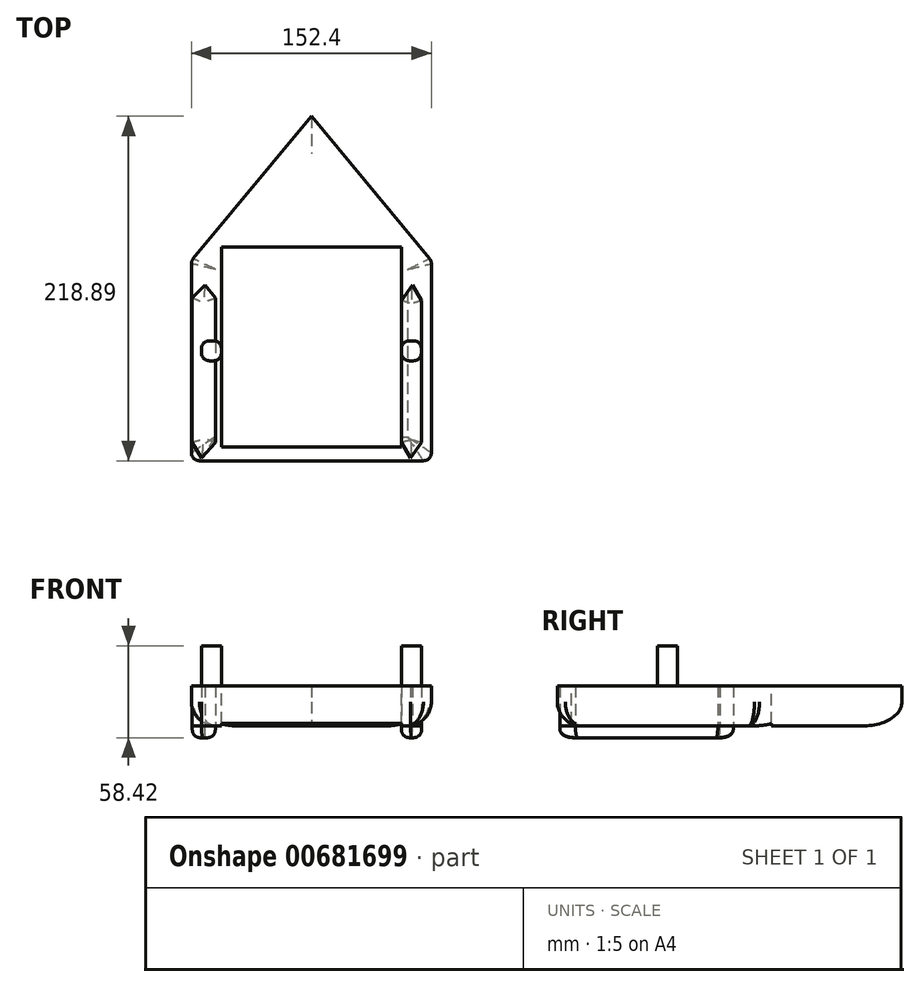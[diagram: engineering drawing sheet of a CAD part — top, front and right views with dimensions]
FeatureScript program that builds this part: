
annotation { "Feature Type Name" : "Feature", "Feature Type Description" : "" }
export const myFeature = defineFeature(function(context is Context, id is Id, definition is map)
    precondition{}
    {
        {
            var Q0;
            Q0=qCreatedBy(makeId("Top.planeOp"),FACE);
            var sketch = newSketch(context, id + "F0", { "sketchPlane" : qUnion([Q0])});
            skLineSegment(sketch, "E0.bottom", {"start": v(-152.4, 91.7) * mm, "end": v(0, 91.7) * mm});
            skLineSegment(sketch, "E0.top", {"start": v(-152.4, -35.3) * mm, "end": v(0, -35.3) * mm});
            skLineSegment(sketch, "E0.left", {"start": v(-152.4, 91.7) * mm, "end": v(-152.4, -35.3) * mm});
            skLineSegment(sketch, "E0.right", {"start": v(0, 91.7) * mm, "end": v(0, -35.3) * mm});
            skLineSegment(sketch, "E1", {"start": v(-76.2, 183.59) * mm, "end": v(-152.4, 91.7) * mm});
            skPoint(sketch, "E1.startSnap0", {"position": v(-76.2, 91.7) * mm});
            skLineSegment(sketch, "E2", {"start": v(-76.2, 183.59) * mm, "end": v(0, 91.7) * mm});
            skSolve(sketch);
        }
        {
            var Q0;
            Q0 = qSketchRegion(id + "F0", true);
            extrude(context, id + "F1", {"entities" : qUnion([Q0]), "depth" : 25.4 * mm, "offsetDistance" : 25.4 * mm});
        }
        {
            var Q0;
            Q0=makeQuery(id+"F1.opExtrude","SWEPT_EDGE",EDGE,{"disambiguationData":[OSD([sQuery(id+"F0.wireOp",EDGE,"E0.bottom"),sQuery(id+"F0.wireOp",EDGE,"E0.right")])]});
            var Q1;
            Q1=makeQuery(id+"F1.opExtrude","SWEPT_EDGE",EDGE,{"disambiguationData":[OSD([sQuery(id+"F0.wireOp",EDGE,"E0.bottom"),sQuery(id+"F0.wireOp",EDGE,"E0.left")])]});
            fillet(context, id + "F2", {"entities" : qUnion([Q0, Q1]), "radius" : 5.08 * mm, "tangentPropagation" : true, "allowEdgeOverflow" : false});
        }
        {
            var Q0;
            Q0=makeQuery(id+"F1.opExtrude","SWEPT_EDGE",EDGE,{"disambiguationData":[OSD([sQuery(id+"F0.wireOp",EDGE,"E0.top"),sQuery(id+"F0.wireOp",EDGE,"E0.right")])]});
            var Q1;
            Q1=makeQuery(id+"F1.opExtrude","SWEPT_EDGE",EDGE,{"disambiguationData":[OSD([sQuery(id+"F0.wireOp",EDGE,"E0.top"),sQuery(id+"F0.wireOp",EDGE,"E0.left")])]});
            fillet(context, id + "F3", {"entities" : qUnion([Q0, Q1]), "radius" : 5.08 * mm, "tangentPropagation" : true, "allowEdgeOverflow" : false});
        }
        {
            var Q0;
            Q0=makeQuery(id+"F1.opExtrude","CAP_EDGE",EDGE,{"disambiguationData":[OSD([sQuery(id+"F0.wireOp",EDGE,"E2")])],"isStart":true});
            fillet(context, id + "F4", {"entities" : qUnion([Q0]), "radius" : 15.24 * mm, "tangentPropagation" : true, "allowEdgeOverflow" : false});
        }
        {
            var Q0;
            Q0=makeQuery(id+"F1.opExtrude","CAP_FACE",FACE,{"disambiguationData":[OSD([sQuery(id+"F0.wireOp",EDGE,"E0.top"),sQuery(id+"F0.wireOp",EDGE,"E0.left"),sQuery(id+"F0.wireOp",EDGE,"E0.right"),sQuery(id+"F0.wireOp",EDGE,"E1"),sQuery(id+"F0.wireOp",EDGE,"E2")])],"isStart":false});
            var sketch = newSketch(context, id + "F5", { "sketchPlane" : qUnion([Q0])});
            skLineSegment(sketch, "E3.bottom", {"start": v(-133.35, 100.59) * mm, "end": v(-19.05, 100.59) * mm});
            skLineSegment(sketch, "E3.top", {"start": v(-133.35, -26.41) * mm, "end": v(-19.05, -26.41) * mm});
            skLineSegment(sketch, "E3.left", {"start": v(-133.35, 100.59) * mm, "end": v(-133.35, -26.41) * mm});
            skLineSegment(sketch, "E3.right", {"start": v(-19.05, 100.59) * mm, "end": v(-19.05, -26.41) * mm});
            skLineSegment(sketch, "E4", {"start": v(-76.2, 100.59) * mm, "end": v(-76.2, -26.41) * mm, "construction": true});
            skSolve(sketch);
        }
        {
            var Q0;
            Q0 = qSketchRegion(id + "F5", true);
            extrude(context, id + "F6", {"entities" : qUnion([Q0]), "operationType" : NewBodyOperationType.REMOVE, "oppositeDirection" : true, "depth" : 55.63 * mm, "offsetDistance" : 25.4 * mm});
        }
        {
            var Q0;
            Q0=makeQuery(id+"F1.opExtrude","CAP_FACE",FACE,{"disambiguationData":[OSD([sQuery(id+"F0.wireOp",EDGE,"E0.top"),sQuery(id+"F0.wireOp",EDGE,"E0.left"),sQuery(id+"F0.wireOp",EDGE,"E0.right"),sQuery(id+"F0.wireOp",EDGE,"E1"),sQuery(id+"F0.wireOp",EDGE,"E2")])],"isStart":false});
            var sketch = newSketch(context, id + "F7", { "sketchPlane" : qUnion([Q0])});
            skLineSegment(sketch, "E5.bottom", {"start": v(-133.35, 40.9) * mm, "end": v(-146.05, 40.9) * mm});
            skLineSegment(sketch, "E5.top", {"start": v(-133.35, 28.2) * mm, "end": v(-146.05, 28.2) * mm});
            skLineSegment(sketch, "E5.left", {"start": v(-133.35, 40.9) * mm, "end": v(-133.35, 28.2) * mm});
            skLineSegment(sketch, "E5.right", {"start": v(-146.05, 40.9) * mm, "end": v(-146.05, 28.2) * mm});
            skLineSegment(sketch, "E6.bottom", {"start": v(-19.05, 40.9) * mm, "end": v(-6.35, 40.9) * mm});
            skLineSegment(sketch, "E6.top", {"start": v(-19.05, 28.2) * mm, "end": v(-6.35, 28.2) * mm});
            skLineSegment(sketch, "E6.left", {"start": v(-19.05, 40.9) * mm, "end": v(-19.05, 28.2) * mm});
            skLineSegment(sketch, "E6.right", {"start": v(-6.35, 40.9) * mm, "end": v(-6.35, 28.2) * mm});
            skSolve(sketch);
        }
        {
            var Q0;
            Q0 = qSketchRegion(id + "F7", true);
            extrude(context, id + "F8", {"entities" : qUnion([Q0]), "operationType" : NewBodyOperationType.ADD, "depth" : 25.4 * mm, "offsetDistance" : 25.4 * mm});
        }
        {
            var Q0;
            Q0=makeQuery(id+"F8.opExtrude","SWEPT_EDGE",EDGE,{"disambiguationData":[OSD([sQuery(id+"F7.wireOp",EDGE,"E5.bottom"),sQuery(id+"F7.wireOp",EDGE,"E5.right")])]});
            var Q1;
            Q1=makeQuery(id+"F8.opExtrude","SWEPT_EDGE",EDGE,{"disambiguationData":[OSD([sQuery(id+"F7.wireOp",EDGE,"E5.top"),sQuery(id+"F7.wireOp",EDGE,"E5.right")])]});
            var Q2;
            Q2=makeQuery(id+"F8.opExtrude","SWEPT_EDGE",EDGE,{"disambiguationData":[OSD([sQuery(id+"F5.wireOp",EDGE,"E3.left"),sQuery(id+"F7.wireOp",EDGE,"E5.top"),sQuery(id+"F7.wireOp",EDGE,"E5.left")])]});
            var Q3;
            Q3=makeQuery(id+"F8.opExtrude","SWEPT_EDGE",EDGE,{"disambiguationData":[OSD([sQuery(id+"F5.wireOp",EDGE,"E3.left"),sQuery(id+"F7.wireOp",EDGE,"E5.bottom"),sQuery(id+"F7.wireOp",EDGE,"E5.left")])]});
            fillet(context, id + "F9", {"entities" : qUnion([Q0, Q1, Q2, Q3]), "radius" : 5.08 * mm, "tangentPropagation" : true, "allowEdgeOverflow" : false});
        }
        {
            var Q0;
            Q0=makeQuery(id+"F8.opExtrude","SWEPT_EDGE",EDGE,{"disambiguationData":[OSD([sQuery(id+"F7.wireOp",EDGE,"E6.top"),sQuery(id+"F7.wireOp",EDGE,"E6.right")])]});
            var Q1;
            Q1=makeQuery(id+"F8.opExtrude","SWEPT_EDGE",EDGE,{"disambiguationData":[OSD([sQuery(id+"F7.wireOp",EDGE,"E6.bottom"),sQuery(id+"F7.wireOp",EDGE,"E6.right")])]});
            var Q2;
            Q2=makeQuery(id+"F8.opExtrude","SWEPT_EDGE",EDGE,{"disambiguationData":[OSD([sQuery(id+"F5.wireOp",EDGE,"E3.right"),sQuery(id+"F7.wireOp",EDGE,"E6.top"),sQuery(id+"F7.wireOp",EDGE,"E6.left")])]});
            var Q3;
            Q3=makeQuery(id+"F8.opExtrude","SWEPT_EDGE",EDGE,{"disambiguationData":[OSD([sQuery(id+"F5.wireOp",EDGE,"E3.right"),sQuery(id+"F7.wireOp",EDGE,"E6.bottom"),sQuery(id+"F7.wireOp",EDGE,"E6.left")])]});
            fillet(context, id + "F10", {"entities" : qUnion([Q0, Q1, Q2, Q3]), "radius" : 5.08 * mm, "tangentPropagation" : true, "allowEdgeOverflow" : false});
        }
        {
            var Q0;
            Q0=qCreatedBy(makeId("Top.planeOp"),FACE);
            var sketch = newSketch(context, id + "F11", { "sketchPlane" : qUnion([Q0])});
            skLineSegment(sketch, "E7", {"start": v(-13.13, -33.57) * mm, "end": v(-19.05, -23.7) * mm});
            skLineSegment(sketch, "E8", {"start": v(-19.05, -23.7) * mm, "end": v(-19.05, 66.55) * mm});
            skLineSegment(sketch, "E9", {"start": v(-19.05, 66.55) * mm, "end": v(-12.15, 76.4) * mm});
            skLineSegment(sketch, "E10", {"start": v(-12.15, 76.4) * mm, "end": v(-6.23, 66.55) * mm});
            skLineSegment(sketch, "E11", {"start": v(-6.23, 66.55) * mm, "end": v(-6.23, -23.7) * mm});
            skLineSegment(sketch, "E12", {"start": v(-6.23, -23.7) * mm, "end": v(-13.13, -33.57) * mm});
            skLineSegment(sketch, "E13", {"start": v(-143.66, 76.4) * mm, "end": v(-137.24, 68.04) * mm});
            skLineSegment(sketch, "E14", {"start": v(-137.24, 68.04) * mm, "end": v(-137.24, -23.7) * mm});
            skLineSegment(sketch, "E15", {"start": v(-137.24, -23.7) * mm, "end": v(-145.92, -33.57) * mm});
            skLineSegment(sketch, "E16", {"start": v(-145.92, -33.57) * mm, "end": v(-151.84, -23.7) * mm});
            skLineSegment(sketch, "E17", {"start": v(-151.84, -23.7) * mm, "end": v(-151.84, 68.04) * mm});
            skLineSegment(sketch, "E18", {"start": v(-151.84, 68.04) * mm, "end": v(-143.66, 76.4) * mm});
            skSolve(sketch);
        }
        {
            var Q0;
            Q0 = qSketchRegion(id + "F11", true);
            extrude(context, id + "F12", {"entities" : qUnion([Q0]), "operationType" : NewBodyOperationType.ADD, "oppositeDirection" : true, "depth" : 7.62 * mm, "offsetDistance" : 25.4 * mm});
        }
        {
            var Q0;
            Q0=makeQuery(id+"F12.opExtrude","CAP_EDGE",EDGE,{"disambiguationData":[OSD([sQuery(id+"F11.wireOp",EDGE,"tmOqJ6vF-TFOI-Q0Wm-q9Of-ddxzmajuP2ZM")])],"isStart":false});
            var Q1;
            Q1=makeQuery(id+"F12.opExtrude","CAP_EDGE",EDGE,{"disambiguationData":[OSD([sQuery(id+"F11.wireOp",EDGE,"FEyd7jUY-jYuC-rwOw-b4N0-UmRakfQqYA6a")])],"isStart":false});
            var Q2;
            Q2=makeQuery(id+"F12.opExtrude","CAP_EDGE",EDGE,{"disambiguationData":[OSD([sQuery(id+"F11.wireOp",EDGE,"0Ef5M7Fk-ZdtT-fkvN-d2lG-GnsX84KVUI3h")])],"isStart":false});
            var Q3;
            Q3=makeQuery(id+"F12.opExtrude","CAP_EDGE",EDGE,{"disambiguationData":[OSD([sQuery(id+"F11.wireOp",EDGE,"4UmGNkGb-MqP5-pd6F-RyAR-tyNyMdDMaayv")])],"isStart":false});
            var Q4;
            Q4=makeQuery(id+"F12.opExtrude","CAP_EDGE",EDGE,{"disambiguationData":[OSD([sQuery(id+"F11.wireOp",EDGE,"sYMeEOHT-bmQm-pcyd-grk8-qopyy1O8IgnV")])],"isStart":false});
            var Q5;
            Q5=makeQuery(id+"F12.opExtrude","CAP_EDGE",EDGE,{"disambiguationData":[OSD([sQuery(id+"F11.wireOp",EDGE,"eJxFwoDH-r6O3-mrbK-mLOy-aVpLiHh0mkwR")])],"isStart":false});
            var Q6;
            Q6=makeQuery(id+"F12.opExtrude","CAP_EDGE",EDGE,{"disambiguationData":[OSD([sQuery(id+"F11.wireOp",EDGE,"E9")])],"isStart":false});
            var Q7;
            Q7=makeQuery(id+"F12.opExtrude","CAP_EDGE",EDGE,{"disambiguationData":[OSD([sQuery(id+"F11.wireOp",EDGE,"E10")])],"isStart":false});
            var Q8;
            Q8=makeQuery(id+"F12.opExtrude","CAP_EDGE",EDGE,{"disambiguationData":[OSD([sQuery(id+"F11.wireOp",EDGE,"E7")])],"isStart":false});
            var Q9;
            Q9=makeQuery(id+"F12.opExtrude","CAP_EDGE",EDGE,{"disambiguationData":[OSD([sQuery(id+"F11.wireOp",EDGE,"E11")])],"isStart":false});
            var Q10;
            Q10=makeQuery(id+"F12.opExtrude","CAP_EDGE",EDGE,{"disambiguationData":[OSD([sQuery(id+"F11.wireOp",EDGE,"E8")])],"isStart":false});
            var Q11;
            Q11=makeQuery(id+"F12.opExtrude","CAP_EDGE",EDGE,{"disambiguationData":[OSD([sQuery(id+"F11.wireOp",EDGE,"E12")])],"isStart":false});
            fillet(context, id + "F13", {"entities" : qUnion([Q0, Q1, Q2, Q3, Q4, Q5, Q6, Q7, Q8, Q9, Q10, Q11]), "radius" : 5.08 * mm, "tangentPropagation" : true, "allowEdgeOverflow" : false});
        }
        {
            var Q0;
            Q0 = qSketchRegion(id + "F11", true);
            extrude(context, id + "F14", {"entities" : qUnion([Q0]), "depth" : 25.4 * mm, "offsetDistance" : 25.4 * mm});
        }
        {
            var Q0;
            Q0=makeQuery(id+"F12.opExtrude","CAP_EDGE",EDGE,{"disambiguationData":[OSD([sQuery(id+"F11.wireOp",EDGE,"E14")])],"isStart":false});
            var Q1;
            Q1=makeQuery(id+"F12.opExtrude","CAP_EDGE",EDGE,{"disambiguationData":[OSD([sQuery(id+"F11.wireOp",EDGE,"E13")])],"isStart":false});
            var Q2;
            Q2=makeQuery(id+"F12.opExtrude","CAP_EDGE",EDGE,{"disambiguationData":[OSD([sQuery(id+"F11.wireOp",EDGE,"E17")])],"isStart":false});
            var Q3;
            Q3=makeQuery(id+"F12.opExtrude","CAP_EDGE",EDGE,{"disambiguationData":[OSD([sQuery(id+"F11.wireOp",EDGE,"E16")])],"isStart":false});
            var Q4;
            Q4=makeQuery(id+"F12.opExtrude","CAP_EDGE",EDGE,{"disambiguationData":[OSD([sQuery(id+"F11.wireOp",EDGE,"E15")])],"isStart":false});
            var Q5;
            Q5=makeQuery(id+"F12.opExtrude","CAP_EDGE",EDGE,{"disambiguationData":[OSD([sQuery(id+"F11.wireOp",EDGE,"E18")])],"isStart":false});
            fillet(context, id + "F15", {"entities" : qUnion([Q0, Q1, Q2, Q3, Q4, Q5]), "radius" : 5.08 * mm, "tangentPropagation" : true, "allowEdgeOverflow" : false});
        }
    });
